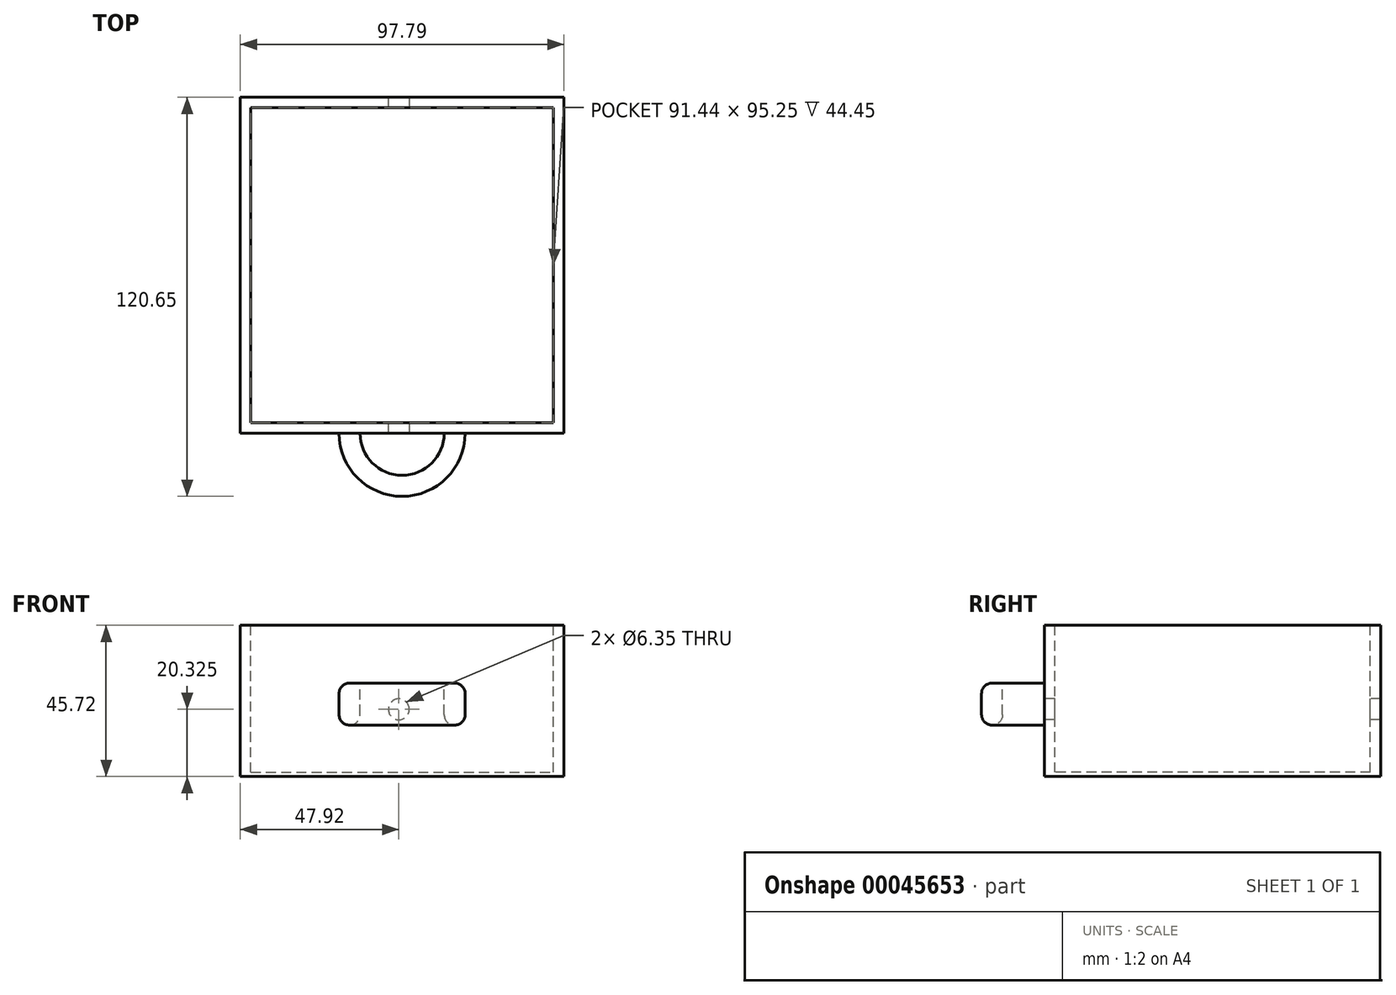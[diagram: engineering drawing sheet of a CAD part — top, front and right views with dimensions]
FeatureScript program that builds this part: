
annotation { "Feature Type Name" : "Feature", "Feature Type Description" : "" }
export const myFeature = defineFeature(function(context is Context, id is Id, definition is map)
    precondition{}
    {
        {
            var Q0;
            Q0=qCreatedBy(makeId("Front.planeOp"),FACE);
            var sketch = newSketch(context, id + "F0", { "sketchPlane" : qUnion([Q0])});
            skLineSegment(sketch, "E0.bottom", {"start": v(-33.41, 27.52) * mm, "end": v(64.38, 27.52) * mm});
            skLineSegment(sketch, "E0.top", {"start": v(-33.41, -18.2) * mm, "end": v(64.38, -18.2) * mm});
            skLineSegment(sketch, "E0.left", {"start": v(-33.41, 27.52) * mm, "end": v(-33.41, -18.2) * mm});
            skLineSegment(sketch, "E0.right", {"start": v(64.38, 27.52) * mm, "end": v(64.38, -18.2) * mm});
            skSolve(sketch);
        }
        {
            var Q0;
            Q0=qSketchRegion(id+"F0",true);
            extrude(context, id + "F1", {"entities" : qUnion([Q0]), "oppositeDirection" : true, "depth" : 101.6 * mm});
        }
        {
            var Q0;
            Q0=makeQuery(id+"F1.opExtrude","SWEPT_FACE",FACE,{"disambiguationData":[OSD([sQuery(id+"F0.wireOp",EDGE,"E0.bottom")])]});
            var sketch = newSketch(context, id + "F2", { "sketchPlane" : qUnion([Q0])});
            skLineSegment(sketch, "E1.bottom", {"start": v(-30.24, 98.43) * mm, "end": v(61.2, 98.43) * mm});
            skLineSegment(sketch, "E1.top", {"start": v(-30.24, 3.17) * mm, "end": v(61.2, 3.18) * mm});
            skLineSegment(sketch, "E1.left", {"start": v(-30.24, 98.43) * mm, "end": v(-30.24, 3.17) * mm});
            skLineSegment(sketch, "E1.right", {"start": v(61.2, 98.43) * mm, "end": v(61.2, 3.18) * mm});
            skSolve(sketch);
        }
        {
            var Q0;
            Q0=qSketchRegion(id+"F2",true);
            extrude(context, id + "F3", {"entities" : qUnion([Q0]), "operationType" : NewBodyOperationType.REMOVE, "oppositeDirection" : true, "depth" : 44.45 * mm});
        }
        {
            var Q0;
            Q0=makeQuery(id+"F1.opExtrude","CAP_FACE",FACE,{"disambiguationData":[OSD([sQuery(id+"F0.wireOp",EDGE,"E0.bottom"),sQuery(id+"F0.wireOp",EDGE,"E0.top"),sQuery(id+"F0.wireOp",EDGE,"E0.left"),sQuery(id+"F0.wireOp",EDGE,"E0.right")])],"isStart":true});
            var sketch = newSketch(context, id + "F4", { "sketchPlane" : qUnion([Q0])});
            skLineSegment(sketch, "E2.bottom", {"start": v(-3.57, 10.06) * mm, "end": v(34.53, 10.06) * mm});
            skLineSegment(sketch, "E2.top", {"start": v(-3.57, -2.64) * mm, "end": v(34.53, -2.64) * mm});
            skLineSegment(sketch, "E2.left", {"start": v(-3.57, 10.06) * mm, "end": v(-3.57, -2.64) * mm});
            skLineSegment(sketch, "E2.right", {"start": v(34.53, 10.06) * mm, "end": v(34.53, -2.64) * mm});
            skLineSegment(sketch, "E3", {"start": v(-3.57, 3.71) * mm, "end": v(34.53, 3.71) * mm});
            skLineSegment(sketch, "E4", {"start": v(15.48, 10.06) * mm, "end": v(15.48, -2.64) * mm});
            skPoint(sketch, "E5", {"position": v(15.48, -18.2) * mm});
            skSolve(sketch);
        }
        {
            var Q0;
            {var subQ3=sQuery(id+"F4.wireOp",EDGE,"E2.bottom");var subQ5=sQuery(id+"F4.wireOp",EDGE,"E2.left");var subQ7=makeQuery(id+"F4.imprint","INTERSECT",VERTEX,{"derivedFrom":[subQ3,subQ5]});Q0=makeQuery(id+"F4.imprint","IMPRINT",FACE,{"disambiguationData":[TD([[makeQuery(id+"F4.imprint","IMPRINT",EDGE,{"disambiguationData":[TD([[subQ7,-1.0]])],"derivedFrom":subQ3}),-1.0]])]});}
            var Q1;
            {var subQ3=sQuery(id+"F4.wireOp",EDGE,"E2.top");var subQ5=sQuery(id+"F4.wireOp",EDGE,"E2.left");var subQ7=makeQuery(id+"F4.imprint","INTERSECT",VERTEX,{"derivedFrom":[subQ3,subQ5]});Q1=makeQuery(id+"F4.imprint","IMPRINT",FACE,{"disambiguationData":[TD([[makeQuery(id+"F4.imprint","IMPRINT",EDGE,{"disambiguationData":[TD([[subQ7,-1.0]])],"derivedFrom":subQ3}),1.0]])]});}
            var Q2;
            Q2=sQuery(id+"F4.wireOp",EDGE,"E4");
            revolve(context, id + "F5", {"operationType" : NewBodyOperationType.ADD, "entities" : qUnion([Q0, Q1]), "axis" : qUnion([Q2]), "revolveType" : RevolveType.ONE_DIRECTION, "oppositeDirection" : true, "angle" : 180 * degree});
        }
        {
            var Q0;
            Q0=makeQuery(id+"F5.opRevolve","SWEPT_FACE",FACE,{"disambiguationData":[OSD([sQuery(id+"F4.wireOp",EDGE,"E2.bottom")])]});
            var sketch = newSketch(context, id + "F6", { "sketchPlane" : qUnion([Q0])});
            skLineSegment(sketch, "E6", {"start": v(2.78, 0) * mm, "end": v(28.18, 0) * mm});
            skArc(sketch, "E7", {"start": v(2.78, 0) * mm, "mid": v(15.48, -12.7) * mm, "end": v(28.18, 0) * mm});
            skSolve(sketch);
        }
        {
            var Q0;
            Q0=qSketchRegion(id+"F6",true);
            extrude(context, id + "F7", {"entities" : qUnion([Q0]), "operationType" : NewBodyOperationType.REMOVE, "oppositeDirection" : true, "depth" : 25.4 * mm});
        }
        {
            var Q0;
            Q0=makeQuery(id+"F5.opRevolve","SWEPT_EDGE",EDGE,{"disambiguationData":[OSD([sQuery(id+"F4.wireOp",EDGE,"E2.bottom"),sQuery(id+"F4.wireOp",EDGE,"E2.left")])]});
            var Q1;
            Q1=makeQuery(id+"F7.boolean.opBoolean","COPY",EDGE,{"derivedFrom":makeQuery(id+"F7.opExtrude","CAP_EDGE",EDGE,{"disambiguationData":[OSD([sQuery(id+"F6.wireOp",EDGE,"E7")])],"isStart":true})});
            var Q2;
            Q2=makeQuery(id+"F5.opRevolve","SWEPT_EDGE",EDGE,{"disambiguationData":[OSD([sQuery(id+"F4.wireOp",EDGE,"E2.top"),sQuery(id+"F4.wireOp",EDGE,"E2.left")])]});
            var Q3;
            Q3=makeQuery(id+"F7.boolean.opBoolean","INTERSECT",EDGE,{"derivedFrom":[makeQuery(id+"F5.opRevolve","SWEPT_FACE",FACE,{"disambiguationData":[OSD([sQuery(id+"F4.wireOp",EDGE,"E2.top")])]}),makeQuery(id+"F7.opExtrude","SWEPT_FACE",FACE,{"disambiguationData":[OSD([sQuery(id+"F6.wireOp",EDGE,"E7")])]})]});
            fillet(context, id + "F8", {"entities" : qUnion([Q0, Q1, Q2, Q3]), "radius" : 3.17 * mm, "tangentPropagation" : true, "allowEdgeOverflow" : false});
        }
        {
            var Q0;
            Q0=makeQuery(id+"F7.boolean.opBoolean","MERGE",FACE,{"derivedFrom":[makeQuery(id+"F1.opExtrude","CAP_FACE",FACE,{"disambiguationData":[OSD([sQuery(id+"F0.wireOp",EDGE,"E0.bottom"),sQuery(id+"F0.wireOp",EDGE,"E0.top"),sQuery(id+"F0.wireOp",EDGE,"E0.left"),sQuery(id+"F0.wireOp",EDGE,"E0.right")])],"isStart":true}),makeQuery(id+"F7.opExtrude","SWEPT_FACE",FACE,{"disambiguationData":[OSD([sQuery(id+"F6.wireOp",EDGE,"E6")])]})]});
            var sketch = newSketch(context, id + "F9", { "sketchPlane" : qUnion([Q0])});
            skPoint(sketch, "E8", {"position": v(14.5, 2.12) * mm});
            skSolve(sketch);
        }
        {
            var Q0;
            Q0=sQuery(id+"F9.wireOp",VERTEX,"E8");
            var Q1;
            Q1=makeQuery(id+"F1.opExtrude","SWEPT_BODY",BODY,{"disambiguationData":[OSD([sQuery(id+"F0.wireOp",EDGE,"E0.bottom"),sQuery(id+"F0.wireOp",EDGE,"E0.top"),sQuery(id+"F0.wireOp",EDGE,"E0.left"),sQuery(id+"F0.wireOp",EDGE,"E0.right")])]});
            hole(context, id + "F10", {"style" : HoleStyle.SIMPLE, "holeDiameter" : 6.35 * mm, "endStyle" : HoleEndStyle.THROUGH, "locations" : qUnion([Q0]), "scope" : qUnion([Q1])});
        }
    });
